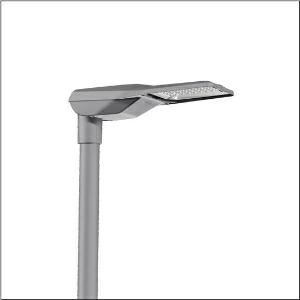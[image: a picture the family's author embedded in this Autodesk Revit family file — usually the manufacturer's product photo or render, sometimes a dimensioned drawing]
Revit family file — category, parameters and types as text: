
# Revit family: streetlight_sl_21_iq_mini___pl52_5xe2h41d08gb_a481
name_source: partatom
category: Lighting Fixtures
units: mm (PartAtom-declared; Revit-internal decimal feet)

## family parameters
Cut with Voids When Loaded = No
Host = Face
Light Source = No
Part Type = Normal
Room Calculation Point = No
Round Connector Dimension = Use Diameter
Shared = No

## types (1)
- --- (1 x LED, 5810 lm, 37.1 W, 4000K)
    Apparent Load = 37 VA
    CIE Flux Codes = 27 59 98 100 100
    Color Rendering = 70
    Color Temperature = 4000K
    Default Elevation = 1800 mm
    Description = Streetlight SL 21 iQ mini, mast luminaire, primary light control with lens, of PMMA, primary optical cover: cover, of toughened safety glass, transparent, light distribution: PL52, light emission: direct distribution, primary light characteristic: asymmetric, installation type: post-top, side-entry, LED, High Power LED, rated luminous flux: 5.810lm, luminous efficacy: 157lm/W, light colour: 740, colour temperature: 4000K, control: Auto-Match, Temp-Guard, Lumen-Switch, Night-Set, Smart-Wire, Light-Fading, Desk-Remote (wireless, voltage-free reading and setting of iQ features in the workshop via application-optimized NFC function/RFID function), optimised constant luminous flux control (CLO 2.0), pre-setting: linear dimming characteristic, mains connection: 220..240V, AC, 50/60Hz, start of lifetime: 37W, end of service life: 39W, reduction: 18W, luminaire housing, of diecast aluminium, powder-coated, Siteco® metallic grey (DB 702S), corrosivity category C5 mid according to DIN EN ISO 12944, please order mast flange separately, inclination adjustable: 0°, 5°, 10°, 15°, sealing non-destructively replaceable, multi-level sealing system, length: 628mm, width: 235mm, height: 110mm, mast flange for spigot size: 42mm (side-entry): 5XC10008XM4, 60/48mm (side-entry/post-top): 5XC10108XM2, 76/60mm (side-entry/post-top): 5XC10108XM1, protection rating (complete): IP66, insulation class (complete): insulation class II (safety insulation), certification: CE, ENEC, ENEC+, VDE, impact resistance: IK09, permissible operating ambient temperature for outdoor applications: -40..+50°C, standard-compliant lighting for roads and squares, packaging unit: 1 piece

Light Distribution: PL52
    Height = 110 mm
    Lamp = 1 x LED
    Lamp Light Flux = 5810 lm
    Lamp Power = 37.1 W
    Lamp count = 1
    Length = 625 mm
    Luminous efficacy = 157 lm/W
    Manufacturer = Siteco
    ModVariant = No
    Model = 5XE2H41D08GB
    Number of Poles = 1
    OnlyDefault = Yes
    Power Factor = 1
    Product Name = Streetlight SL 21 iQ mini | PL52
    Product group = mast luminaire | pylon top
    ProductGroupID = 6100
    Protection Class = Protection class II
    Protection Degree = IP 66
    RLX_Detail_Level = 1
    RLX_Emergency_Light_Flux = 0 lm
    RLX_Emergency_Type = 0
    RLX_Emergency_Type_DB = No
    RlxData = <blob elided: 102373 chars, md5=f119d918>
    Socket = socket
    Standby Power = 0 W
    System Light Flux = 5810 lm
    System Power = 37 W
    Type Comments = factory setting: luminous flux: 100 % | dim-lin: 254 | 385 mA
    Type Image = l_1003519.jpg
    URL = http://relux.com
    VarID = @adj_162661
    Voltage = 0 V
    Weight = 0.00 kg
    Width = 234 mm

## geometry (parser evidence)
native form markers: Blend x4, Sweep x10
no freeform markers — native parametric forms only
